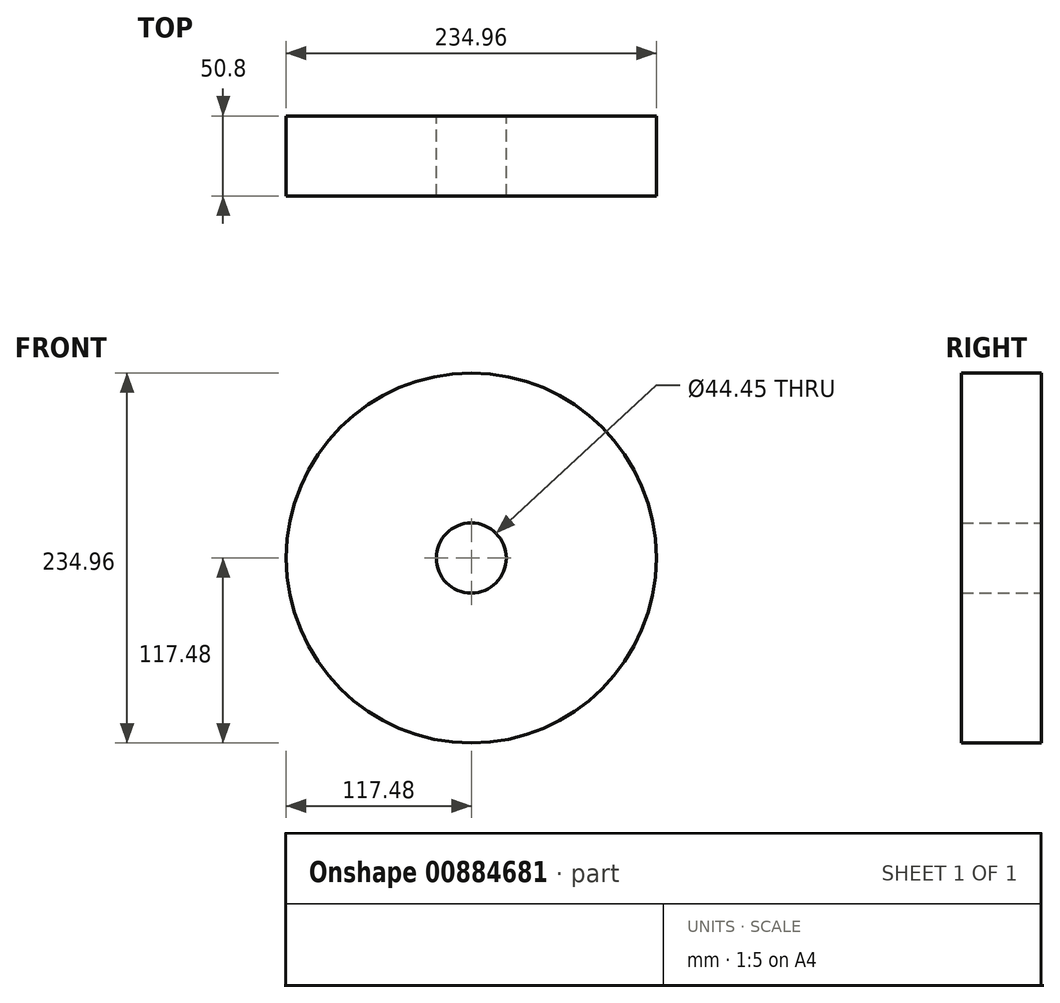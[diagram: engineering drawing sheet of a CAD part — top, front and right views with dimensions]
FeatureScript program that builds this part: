
annotation { "Feature Type Name" : "Feature", "Feature Type Description" : "" }
export const myFeature = defineFeature(function(context is Context, id is Id, definition is map)
    precondition{}
    {
        {
            var Q0;
            Q0=qCreatedBy(makeId("Front.planeOp"),FACE);
            var sketch = newSketch(context, id + "F0", { "sketchPlane" : qUnion([Q0])});
            skCircle(sketch, "E0", {"center": v(0, 0) * mm, "radius": 117.48 * mm});
            skCircle(sketch, "E1", {"center": v(0, 0) * mm, "radius": 22.23 * mm});
            skSolve(sketch);
        }
        {
            var Q0;
            Q0 = qSketchRegion(id + "F0", true);
            var Q1;
            Q1=makeQuery(id+"F0.imprint","IMPRINT",FACE,{"disambiguationData":[TD([[makeQuery(id+"F0.imprint","IMPRINT",EDGE,{"derivedFrom":sQuery(id+"F0.wireOp",EDGE,"E0")}),1.0]])]});
            extrude(context, id + "F1", {"entities" : qUnion([Q0, Q1]), "depth" : 50.8 * mm, "offsetDistance" : 25.4 * mm});
        }
    });
